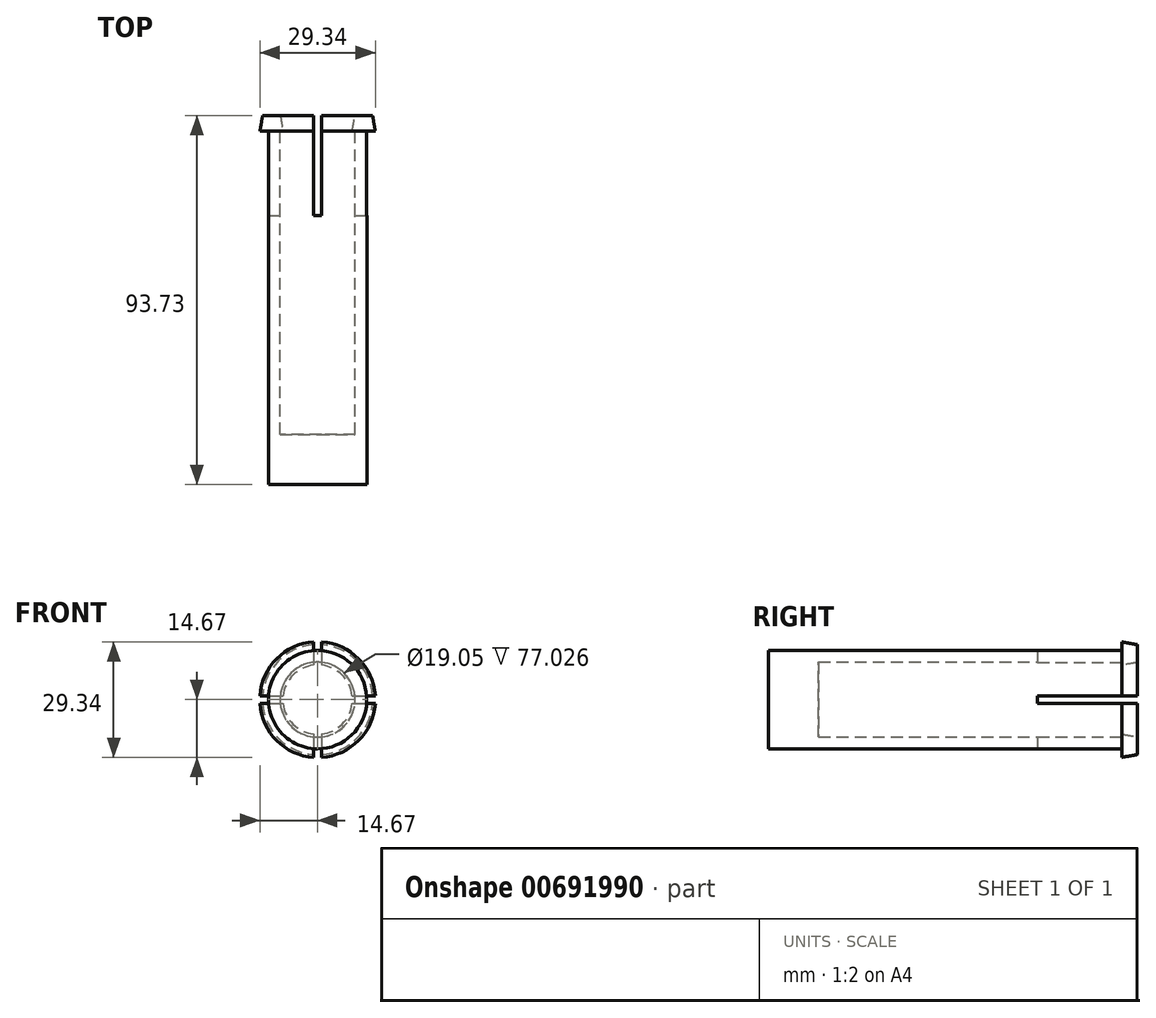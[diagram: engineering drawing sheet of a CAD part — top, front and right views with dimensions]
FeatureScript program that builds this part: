
annotation { "Feature Type Name" : "Feature", "Feature Type Description" : "" }
export const myFeature = defineFeature(function(context is Context, id is Id, definition is map)
    precondition{}
    {
        {
            var Q0;
            Q0=qCreatedBy(makeId("Front.planeOp"),FACE);
            var sketch = newSketch(context, id + "F0", { "sketchPlane" : qUnion([Q0])});
            skCircle(sketch, "E0", {"center": v(0, 0) * mm, "radius": 12.5 * mm});
            skCircle(sketch, "E1", {"center": v(0, 0) * mm, "radius": 9.53 * mm});
            skSolve(sketch);
        }
        {
            var Q0;
            Q0 = qSketchRegion(id + "F0", true);
            extrude(context, id + "F1", {"entities" : qUnion([Q0]), "depth" : 81.03 * mm, "offsetDistance" : 25.4 * mm});
        }
        {
            var Q0;
            Q0=makeQuery(id+"F1.opExtrude","CAP_FACE",FACE,{"disambiguationData":[OSD([sQuery(id+"F0.wireOp",EDGE,"E0")])],"isStart":true});
            var sketch = newSketch(context, id + "F2", { "sketchPlane" : qUnion([Q0])});
            skCircle(sketch, "E2", {"center": v(0, 0) * mm, "radius": 14 * mm});
            skCircle(sketch, "E3.0", {"center": v(0, 0) * mm, "radius": 9.53 * mm});
            skSolve(sketch);
        }
        {
            var Q0;
            Q0 = qSketchRegion(id + "F2", true);
            extrude(context, id + "F3", {"entities" : qUnion([Q0]), "operationType" : NewBodyOperationType.ADD, "oppositeDirection" : true, "depth" : 4 * mm, "offsetDistance" : 25.4 * mm, "hasDraft" : true, "draftAngle" : 10 * degree});
        }
        {
            var Q0;
            Q0=makeQuery(id+"F0.imprint","IMPRINT",FACE,{"disambiguationData":[TD([[makeQuery(id+"F0.imprint","IMPRINT",EDGE,{"derivedFrom":sQuery(id+"F0.wireOp",EDGE,"E0")}),1.0]])]});
            var sketch = newSketch(context, id + "F4", { "sketchPlane" : qUnion([Q0])});
            skLineSegment(sketch, "E4.bottom", {"start": v(-17.5, 1) * mm, "end": v(17.5, 1) * mm});
            skLineSegment(sketch, "E4.top", {"start": v(-17.5, -1) * mm, "end": v(17.5, -1) * mm});
            skLineSegment(sketch, "E4.left", {"start": v(-17.5, 1) * mm, "end": v(-17.5, -1) * mm});
            skLineSegment(sketch, "E4.right", {"start": v(17.5, 1) * mm, "end": v(17.5, -1) * mm});
            skPoint(sketch, "E4.middle", {"position": v(0, 0) * mm});
            skLineSegment(sketch, "E5.bottom", {"start": v(-1, 17.5) * mm, "end": v(1, 17.5) * mm});
            skLineSegment(sketch, "E5.top", {"start": v(-1, -17.5) * mm, "end": v(1, -17.5) * mm});
            skLineSegment(sketch, "E5.left", {"start": v(-1, 17.5) * mm, "end": v(-1, -17.5) * mm});
            skLineSegment(sketch, "E5.right", {"start": v(1, 17.5) * mm, "end": v(1, -17.5) * mm});
            skSolve(sketch);
        }
        {
            var Q0;
            Q0 = qSketchRegion(id + "F4", true);
            extrude(context, id + "F5", {"entities" : qUnion([Q0]), "operationType" : NewBodyOperationType.REMOVE, "depth" : 25.4 * mm, "offsetDistance" : 25.4 * mm});
        }
        {
            var Q0;
            Q0=makeQuery(id+"F1.opExtrude","CAP_FACE",FACE,{"disambiguationData":[OSD([sQuery(id+"F0.wireOp",EDGE,"E0"),sQuery(id+"F0.wireOp",EDGE,"E1")])],"isStart":false});
            var sketch = newSketch(context, id + "F6", { "sketchPlane" : qUnion([Q0])});
            skCircle(sketch, "E6.0", {"center": v(0, 0) * mm, "radius": 12.5 * mm});
            skSolve(sketch);
        }
        {
            var Q0;
            Q0 = qSketchRegion(id + "F6", true);
            extrude(context, id + "F7", {"entities" : qUnion([Q0]), "operationType" : NewBodyOperationType.ADD, "depth" : 12.7 * mm, "offsetDistance" : 25.4 * mm});
        }
    });
